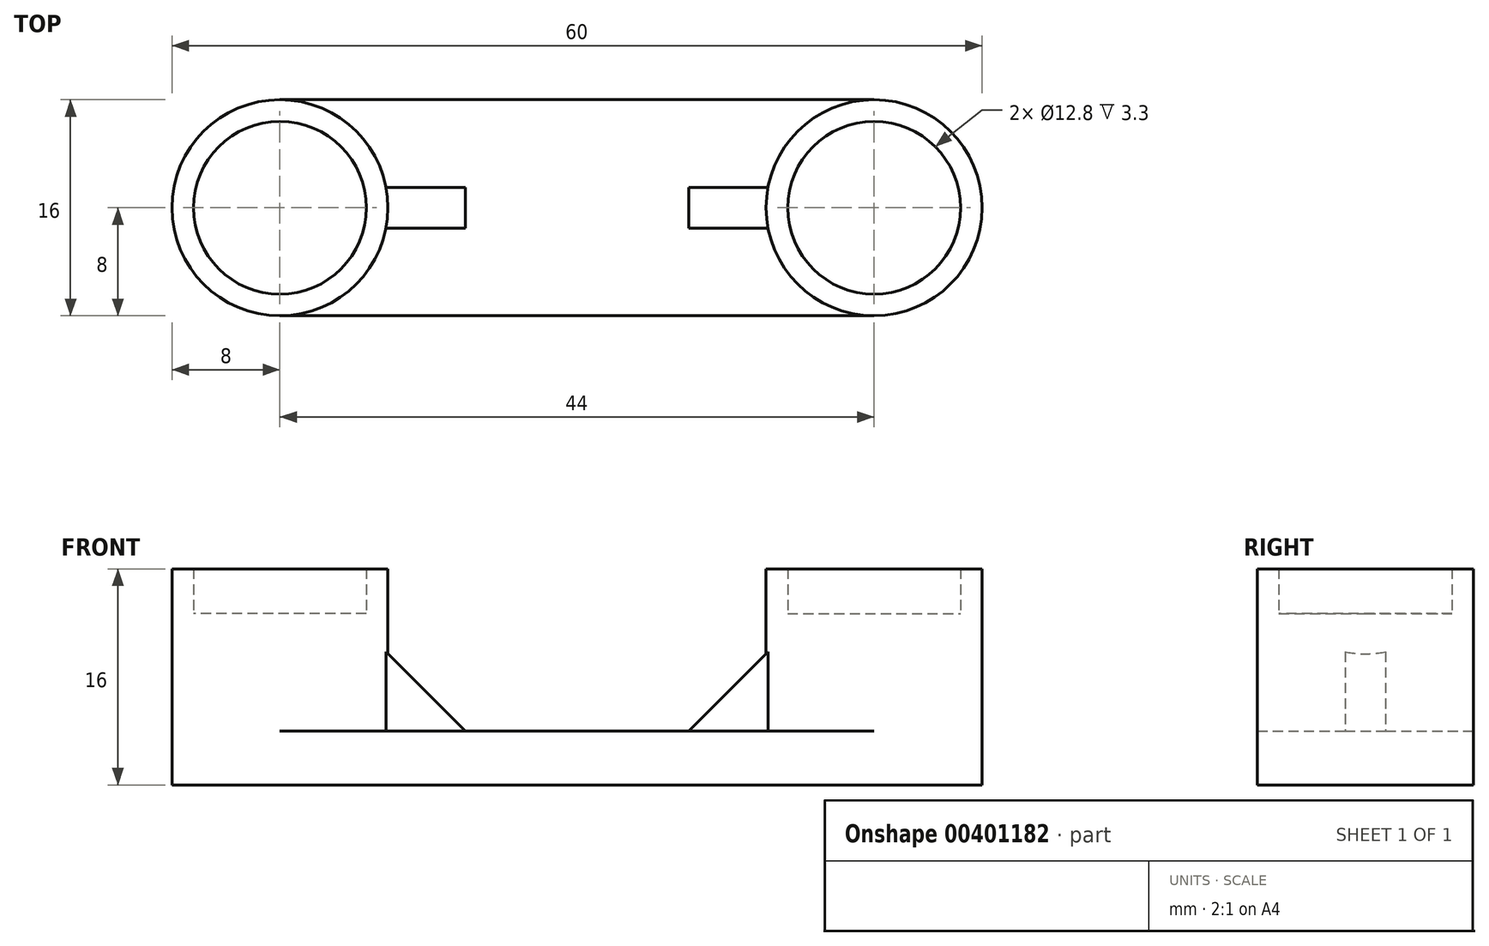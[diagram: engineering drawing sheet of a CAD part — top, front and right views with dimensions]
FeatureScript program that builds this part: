
annotation { "Feature Type Name" : "Feature", "Feature Type Description" : "" }
export const myFeature = defineFeature(function(context is Context, id is Id, definition is map)
    precondition{}
    {
        {
            var Q0;
            Q0=qCreatedBy(makeId("Top.planeOp"),FACE);
            var sketch = newSketch(context, id + "F0", { "sketchPlane" : qUnion([Q0])});
            skLineSegment(sketch, "E0.bottom", {"start": v(-22, 8) * mm, "end": v(0, 8) * mm});
            skLineSegment(sketch, "E0.top", {"start": v(-22, -8) * mm, "end": v(0, -8) * mm});
            skLineSegment(sketch, "E0.right", {"start": v(0, 8) * mm, "end": v(0, -8) * mm});
            skPoint(sketch, "E0.middle", {"position": v(0, 0) * mm});
            skArc(sketch, "E1", {"start": v(-22, 8) * mm, "mid": v(-30, 0) * mm, "end": v(-22, -8) * mm});
            skSolve(sketch);
        }
        {
            var Q0;
            Q0=qCreatedBy(makeId("Top.planeOp"),FACE);
            var sketch = newSketch(context, id + "F1", { "sketchPlane" : qUnion([Q0])});
            skPoint(sketch, "E2.middle", {"position": v(-3.82, 8.34) * mm});
            skCircle(sketch, "E3", {"center": v(-22, 0) * mm, "radius": 6.4 * mm});
            skCircle(sketch, "E4", {"center": v(-22, 0) * mm, "radius": 8 * mm});
            skSolve(sketch);
        }
        {
            var Q0;
            Q0 = qSketchRegion(id + "F1", true);
            extrude(context, id + "F2", {"entities" : qUnion([Q0]), "depth" : 16 * mm});
        }
        {
            var Q0;
            Q0 = qSketchRegion(id + "F0", true);
            extrude(context, id + "F3", {"entities" : qUnion([Q0]), "operationType" : NewBodyOperationType.ADD, "depth" : 4 * mm});
        }
        {
            var Q0;
            Q0=makeQuery(id+"F3.boolean.opBoolean","SPLIT",FACE,{"disambiguationData":[TD([makeQuery(id+"F2.opExtrude","SWEPT_FACE",FACE,{"disambiguationData":[OSD([sQuery(id+"F1.wireOp",EDGE,"E3")])]})])],"derivedFrom":makeQuery(id+"F3.opExtrude","CAP_FACE",FACE,{"disambiguationData":[OSD([sQuery(id+"F0.wireOp",EDGE,"E0.bottom"),sQuery(id+"F0.wireOp",EDGE,"E0.top"),sQuery(id+"F0.wireOp",EDGE,"E0.right"),sQuery(id+"F0.wireOp",EDGE,"E1")])],"isStart":false})});
            extrude(context, id + "F4", {"entities" : qUnion([Q0]), "operationType" : NewBodyOperationType.ADD, "depth" : (16 - 7.3) * mm});
        }
        {
            var Q0;
            Q0=qCreatedBy(makeId("Front.planeOp"),FACE);
            var sketch = newSketch(context, id + "F5", { "sketchPlane" : qUnion([Q0])});
            skLineSegment(sketch, "E5", {"start": v(-14.32, 10.03) * mm, "end": v(-8.27, 4) * mm});
            skLineSegment(sketch, "E6", {"start": v(-8.27, 4) * mm, "end": v(-14.3, 4) * mm});
            skLineSegment(sketch, "E7", {"start": v(-14.3, 4) * mm, "end": v(-14.32, 10.03) * mm});
            skSolve(sketch);
        }
        {
            var Q0;
            Q0 = qSketchRegion(id + "F5", true);
            extrude(context, id + "F6", {"entities" : qUnion([Q0]), "operationType" : NewBodyOperationType.ADD, "endBound" : BoundingType.SYMMETRIC, "depth" : 3 * mm});
        }
        {
            var Q0;
            Q0=makeQuery(id+"F2.opExtrude","SWEPT_BODY",BODY,{"disambiguationData":[OSD([sQuery(id+"F1.wireOp",EDGE,"E3"),sQuery(id+"F1.wireOp",EDGE,"E4")])]});
            var Q1;
            Q1=qCreatedBy(makeId("Right.planeOp"),FACE);
            mirror(context, id + "F7", {"operationType" : NewBodyOperationType.ADD, "entities" : qUnion([Q0]), "mirrorPlane" : qUnion([Q1])});
        }
    });
